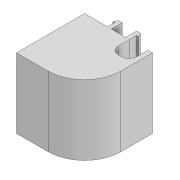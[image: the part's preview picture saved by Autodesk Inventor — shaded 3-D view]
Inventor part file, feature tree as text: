
AUTODESK INVENTOR PART (.ipt)
format: ipt  version: 2021 (Build 250183000, 183)  size: 199,680 bytes
history: native  units: mm
features: other x5, plane x2, extrude x2, sketch x2
ambient origin geometry x8: Origin, YZ Plane, XZ Plane, XY Plane, X Axis, Y Axis, Z Axis, Center Point
bodies: Volumenkörper1 (feature_tree)
feature tree (11):
  other  "Corner_Layout.ipt"
  plane  "Arbeitsebene1"
  other  "Trennen1"
  plane  "Arbeitsebene2"
  other  "Trennen2"
  extrude  "Extrusion1"  [1 undecoded]
  extrude  "Extrusion2"  TaperAngle=0.0deg  [1 undecoded]
  other  "Volumenkörper1::Corner_Layout.ipt"
  other  "Bezeichnung1"
  sketch  "Skizze1"  dims[d0=10.0mm d1=-16.0mm]
  sketch  "Skizze2"  dims[d2=3.5mm d3=0.0mm d4=0.0mm d5=0.0mm d6=0.0mm]
note: 2 required parameter values undecoded (feature->parameter linkage not recoverable at this tier; creation-order binding heuristic only, values carry confidence <= 0.55)
